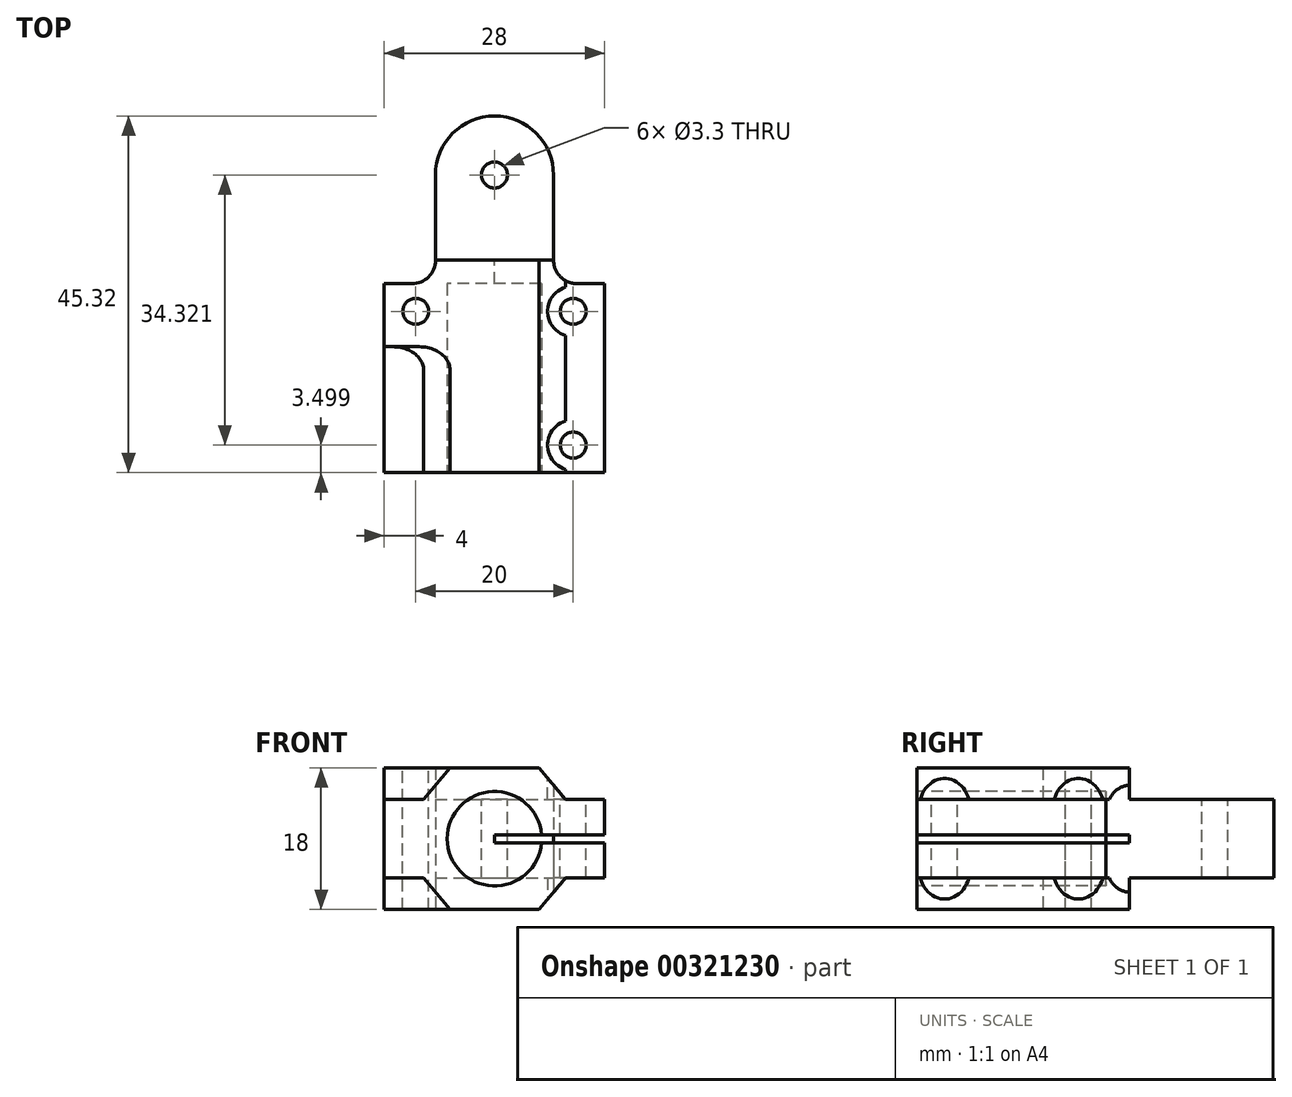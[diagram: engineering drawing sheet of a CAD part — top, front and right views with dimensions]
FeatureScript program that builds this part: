
annotation { "Feature Type Name" : "Feature", "Feature Type Description" : "" }
export const myFeature = defineFeature(function(context is Context, id is Id, definition is map)
    precondition{}
    {
        {
            var Q0;
            Q0=qCreatedBy(makeId("Top.planeOp"),FACE);
            var sketch = newSketch(context, id + "F0", { "sketchPlane" : qUnion([Q0])});
            skCircle(sketch, "E0", {"center": v(0, 0) * mm, "radius": 20 * mm, "construction": true});
            skSolve(sketch);
        }
        {
            var Q0;
            Q0=qCreatedBy(makeId("Top.planeOp"),FACE);
            var sketch = newSketch(context, id + "F1", { "sketchPlane" : qUnion([Q0])});
            skCircle(sketch, "E1", {"center": v(0, 0) * mm, "radius": 7.5 * mm});
            skLineSegment(sketch, "E2", {"start": v(-14, -13.82) * mm, "end": v(-14, -37.82) * mm});
            skLineSegment(sketch, "E3", {"start": v(-14, -37.82) * mm, "end": v(14, -37.82) * mm});
            skLineSegment(sketch, "E4", {"start": v(14, -37.82) * mm, "end": v(14, -13.82) * mm});
            skLineSegment(sketch, "E5", {"start": v(0, 0) * mm, "end": v(0, -37.82) * mm, "construction": true});
            skLineSegment(sketch, "E6", {"start": v(-6, -37.82) * mm, "end": v(-6, -10.4) * mm, "construction": true});
            skCircle(sketch, "E7.0", {"center": v(0, 0) * mm, "radius": 20 * mm, "construction": true});
            skPoint(sketch, "E8", {"position": v(-10, -17.32) * mm});
            skPoint(sketch, "E9.MirrorP", {"position": v(10, -17.32) * mm});
            skPoint(sketch, "E10", {"position": v(-10, -34.32) * mm});
            skPoint(sketch, "E11.MirrorP", {"position": v(10, -34.32) * mm});
            skLineSegment(sketch, "E12", {"start": v(-7.5, 0) * mm, "end": v(-7.5, -13.82) * mm});
            skLineSegment(sketch, "E13", {"start": v(-7.5, -13.82) * mm, "end": v(-14, -13.82) * mm});
            skLineSegment(sketch, "E14", {"start": v(7.5, 0) * mm, "end": v(7.5, -13.82) * mm});
            skLineSegment(sketch, "E15", {"start": v(7.5, -13.82) * mm, "end": v(14, -13.82) * mm});
            skLineSegment(sketch, "E16", {"start": v(-10, -17.32) * mm, "end": v(0, 0) * mm, "construction": true});
            skPoint(sketch, "E17", {"position": v(0, -34.32) * mm});
            skLineSegment(sketch, "E18", {"start": v(0, 0) * mm, "end": v(20, 0) * mm});
            skSolve(sketch);
        }
        {
            var Q0;
            Q0 = qSketchRegion(id + "F1", true);
            extrude(context, id + "F2", {"entities" : qUnion([Q0]), "endBound" : BoundingType.SYMMETRIC, "depth" : 18 * mm});
        }
        {
            var Q0;
            Q0=makeQuery(id+"F2.opExtrude","SWEPT_FACE",FACE,{"disambiguationData":[OSD([sQuery(id+"F1.wireOp",EDGE,"E3")])]});
            var sketch = newSketch(context, id + "F3", { "sketchPlane" : qUnion([Q0])});
            skCircle(sketch, "E19", {"center": v(0, 0) * mm, "radius": 6 * mm});
            skSolve(sketch);
        }
        {
            var Q0;
            Q0=makeQuery(id+"F3.imprint","IMPRINT",FACE,{"disambiguationData":[TD([[makeQuery(id+"F3.imprint","IMPRINT",EDGE,{"derivedFrom":sQuery(id+"F3.wireOp",EDGE,"E19")}),1.0]])]});
            var Q1;
            Q1=sQuery(id+"F3.wireOp",EDGE,"E19");
            extrude(context, id + "F4", {"entities" : qUnion([Q0]), "operationType" : NewBodyOperationType.REMOVE, "surfaceEntities" : qUnion([Q1]), "oppositeDirection" : true, "depth" : 24 * mm});
        }
        {
            var Q0;
            Q0=makeQuery(id+"F2.opExtrude","SWEPT_FACE",FACE,{"disambiguationData":[OSD([sQuery(id+"F1.wireOp",EDGE,"E3")])]});
            var sketch = newSketch(context, id + "F5", { "sketchPlane" : qUnion([Q0])});
            skLineSegment(sketch, "E20", {"start": v(0, 0) * mm, "end": v(0, 22.33) * mm, "construction": true});
            skLineSegment(sketch, "E21", {"start": v(0, 0) * mm, "end": v(-30.07, 0) * mm, "construction": true});
            skPoint(sketch, "E21.endSnap0", {"position": v(-14, 0) * mm});
            skLineSegment(sketch, "E22", {"start": v(5.64, 9) * mm, "end": v(9, 5) * mm});
            skLineSegment(sketch, "E23", {"start": v(9, 5) * mm, "end": v(14, 5) * mm});
            skLineSegment(sketch, "E24", {"start": v(5.64, 9) * mm, "end": v(14, 9) * mm});
            skLineSegment(sketch, "E25", {"start": v(14, 9) * mm, "end": v(14, 5) * mm});
            skLineSegment(sketch, "E26.MirrorCS", {"start": v(-5.64, 9) * mm, "end": v(-9, 5) * mm});
            skLineSegment(sketch, "E27.MirrorCS", {"start": v(-9, 5) * mm, "end": v(-14, 5) * mm});
            skLineSegment(sketch, "E28.MirrorCS", {"start": v(-14, 9) * mm, "end": v(-14, 5) * mm});
            skLineSegment(sketch, "E29.MirrorCS", {"start": v(-5.64, 9) * mm, "end": v(-14, 9) * mm});
            skLineSegment(sketch, "E30.MirrorCS", {"start": v(-5.64, -9) * mm, "end": v(-9, -5) * mm});
            skLineSegment(sketch, "E31.MirrorCS", {"start": v(-5.64, -9) * mm, "end": v(-14, -9) * mm});
            skLineSegment(sketch, "E32.MirrorCS", {"start": v(-14, -9) * mm, "end": v(-14, -5) * mm});
            skLineSegment(sketch, "E33.MirrorCS", {"start": v(-9, -5) * mm, "end": v(-14, -5) * mm});
            skLineSegment(sketch, "E34.MirrorCS", {"start": v(9, -5) * mm, "end": v(14, -5) * mm});
            skLineSegment(sketch, "E35.MirrorCS", {"start": v(5.64, -9) * mm, "end": v(9, -5) * mm});
            skLineSegment(sketch, "E36.MirrorCS", {"start": v(5.64, -9) * mm, "end": v(14, -9) * mm});
            skLineSegment(sketch, "E37.MirrorCS", {"start": v(14, -9) * mm, "end": v(14, -5) * mm});
            skSolve(sketch);
        }
        {
            var Q0;
            Q0=makeQuery(id+"F5.imprint","IMPRINT",FACE,{"disambiguationData":[TD([[makeQuery(id+"F5.imprint","IMPRINT",EDGE,{"derivedFrom":sQuery(id+"F5.wireOp",EDGE,"E22")}),1.0]])]});
            var Q1;
            Q1=makeQuery(id+"F5.imprint","IMPRINT",FACE,{"disambiguationData":[TD([[makeQuery(id+"F5.imprint","IMPRINT",EDGE,{"derivedFrom":sQuery(id+"F5.wireOp",EDGE,"E35.MirrorCS")}),-1.0]])]});
            extrude(context, id + "F6", {"entities" : qUnion([Q0, Q1]), "operationType" : NewBodyOperationType.REMOVE, "endBound" : BoundingType.THROUGH_ALL, "oppositeDirection" : true, "depth" : 30 * mm});
        }
        {
            var Q0;
            Q0=makeQuery(id+"F5.imprint","IMPRINT",FACE,{"disambiguationData":[TD([[makeQuery(id+"F5.imprint","IMPRINT",EDGE,{"derivedFrom":sQuery(id+"F5.wireOp",EDGE,"E26.MirrorCS")}),-1.0]])]});
            var Q1;
            Q1=makeQuery(id+"F5.imprint","IMPRINT",FACE,{"disambiguationData":[TD([[makeQuery(id+"F5.imprint","IMPRINT",EDGE,{"derivedFrom":sQuery(id+"F5.wireOp",EDGE,"E30.MirrorCS")}),1.0]])]});
            extrude(context, id + "F7", {"entities" : qUnion([Q0, Q1]), "operationType" : NewBodyOperationType.REMOVE, "oppositeDirection" : true, "depth" : 16 * mm});
        }
        {
            var Q0;
            Q0=makeQuery(id+"F2.opExtrude","SWEPT_EDGE",EDGE,{"disambiguationData":[OSD([sQuery(id+"F1.wireOp",EDGE,"E14"),sQuery(id+"F1.wireOp",EDGE,"E15")])]});
            var Q1;
            Q1=makeQuery(id+"F2.opExtrude","SWEPT_EDGE",EDGE,{"disambiguationData":[OSD([sQuery(id+"F1.wireOp",EDGE,"E12"),sQuery(id+"F1.wireOp",EDGE,"E13")])]});
            var Q2;
            Q2=makeQuery(id+"F7.boolean.opBoolean","COPY",EDGE,{"derivedFrom":makeQuery(id+"F7.opExtrude","CAP_EDGE",EDGE,{"disambiguationData":[OSD([sQuery(id+"F5.wireOp",EDGE,"E26.MirrorCS")])],"isStart":false})});
            var Q3;
            Q3=makeQuery(id+"F7.boolean.opBoolean","COPY",EDGE,{"derivedFrom":makeQuery(id+"F7.opExtrude","CAP_EDGE",EDGE,{"disambiguationData":[OSD([sQuery(id+"F5.wireOp",EDGE,"E30.MirrorCS")])],"isStart":false})});
            fillet(context, id + "F8", {"entities" : qUnion([Q0, Q1, Q2, Q3]), "radius" : 3 * mm, "tangentPropagation" : true, "allowEdgeOverflow" : false});
        }
        {
            var Q0;
            Q0=makeQuery(id+"F2.opExtrude","SWEPT_FACE",FACE,{"disambiguationData":[OSD([sQuery(id+"F1.wireOp",EDGE,"E14")])]});
            var sketch = newSketch(context, id + "F9", { "sketchPlane" : qUnion([Q0])});
            skLineSegment(sketch, "E38", {"start": v(0, 0) * mm, "end": v(12.2, 0) * mm, "construction": true});
            skLineSegment(sketch, "E39.0", {"start": v(4.94, 9) * mm, "end": v(-37.82, 9) * mm});
            skLineSegment(sketch, "E40.0", {"start": v(-10.82, 6.79) * mm, "end": v(-10.82, -6.79) * mm});
            skLineSegment(sketch, "E41.bottom", {"start": v(-10.82, 5) * mm, "end": v(9.93, 5) * mm});
            skLineSegment(sketch, "E41.top", {"start": v(-10.82, 9) * mm, "end": v(9.93, 9) * mm});
            skLineSegment(sketch, "E41.left", {"start": v(-10.82, 5) * mm, "end": v(-10.82, 9) * mm});
            skLineSegment(sketch, "E41.right", {"start": v(9.93, 5) * mm, "end": v(9.93, 9) * mm});
            skLineSegment(sketch, "E42.MirrorCS", {"start": v(-10.82, -5) * mm, "end": v(9.93, -5) * mm});
            skLineSegment(sketch, "E43.MirrorCS", {"start": v(9.93, -5) * mm, "end": v(9.93, -9) * mm});
            skLineSegment(sketch, "E44.MirrorCS", {"start": v(-10.82, -9) * mm, "end": v(9.93, -9) * mm});
            skLineSegment(sketch, "E45.MirrorCS", {"start": v(-10.82, -5) * mm, "end": v(-10.82, -9) * mm});
            skSolve(sketch);
        }
        {
            var Q0;
            Q0 = qSketchRegion(id + "F9", true);
            extrude(context, id + "F10", {"entities" : qUnion([Q0]), "operationType" : NewBodyOperationType.REMOVE, "endBound" : BoundingType.THROUGH_ALL, "oppositeDirection" : true, "depth" : 25 * mm});
        }
        {
            var Q0;
            Q0=makeQuery(id+"F2.opExtrude","CAP_FACE",FACE,{"disambiguationData":[OSD([sQuery(id+"F1.wireOp",EDGE,"E1"),sQuery(id+"F1.wireOp",EDGE,"FBtvDSVI-ImC7-X96t-MR7d-RFuTRP7ZC0sh"),sQuery(id+"F1.wireOp",EDGE,"E2"),sQuery(id+"F1.wireOp",EDGE,"E3"),sQuery(id+"F1.wireOp",EDGE,"E4"),sQuery(id+"F1.wireOp",EDGE,"JECMxVH1-krey-lWLA-VkQH-IbSMAUhGZjWj")])],"isStart":false});
            var sketch = newSketch(context, id + "F11", { "sketchPlane" : qUnion([Q0])});
            skPoint(sketch, "E46.0", {"position": v(-10, -17.32) * mm});
            skPoint(sketch, "E46.1", {"position": v(-10, -34.32) * mm});
            skPoint(sketch, "E46.2", {"position": v(10, -34.32) * mm});
            skPoint(sketch, "E46.3", {"position": v(10, -17.32) * mm});
            skPoint(sketch, "E47.0", {"position": v(0, 0) * mm});
            skSolve(sketch);
        }
        {
            var Q0;
            Q0=sQuery(id+"F11.wireOp",VERTEX,"E46.2");
            var Q1;
            Q1=sQuery(id+"F11.wireOp",VERTEX,"E46.3");
            var Q2;
            Q2=sQuery(id+"F11.wireOp",VERTEX,"E47.0");
            var Q3;
            Q3=sQuery(id+"F11.wireOp",VERTEX,"E46.0");
            var Q4;
            Q4=makeQuery(id+"F2.opExtrude","SWEPT_BODY",BODY,{"disambiguationData":[OSD([sQuery(id+"F1.wireOp",EDGE,"E1"),sQuery(id+"F1.wireOp",EDGE,"FBtvDSVI-ImC7-X96t-MR7d-RFuTRP7ZC0sh"),sQuery(id+"F1.wireOp",EDGE,"E2"),sQuery(id+"F1.wireOp",EDGE,"E3"),sQuery(id+"F1.wireOp",EDGE,"E4"),sQuery(id+"F1.wireOp",EDGE,"JECMxVH1-krey-lWLA-VkQH-IbSMAUhGZjWj")])]});
            hole(context, id + "F12", {"style" : HoleStyle.C_BORE, "endStyle" : HoleEndStyle.THROUGH, "holeDiameter" : 3.3 * mm, "cBoreDiameter" : 6.5 * mm, "cBoreDepth" : 0 * mm, "tappedDepth" : 1.2 * mm, "tapClearance" : 3, "locations" : qUnion([Q0, Q1, Q2, Q3]), "scope" : qUnion([Q4])});
        }
        {
            var Q0;
            Q0=makeQuery(id+"F2.opExtrude","CAP_FACE",FACE,{"disambiguationData":[OSD([sQuery(id+"F1.wireOp",EDGE,"E1"),sQuery(id+"F1.wireOp",EDGE,"E2"),sQuery(id+"F1.wireOp",EDGE,"E3"),sQuery(id+"F1.wireOp",EDGE,"E4"),sQuery(id+"F1.wireOp",EDGE,"E12"),sQuery(id+"F1.wireOp",EDGE,"E13"),sQuery(id+"F1.wireOp",EDGE,"E14"),sQuery(id+"F1.wireOp",EDGE,"E15")])],"isStart":true});
            var sketch = newSketch(context, id + "F13", { "sketchPlane" : qUnion([Q0])});
            skPoint(sketch, "E48.0", {"position": v(-10, 34.32) * mm});
            skPoint(sketch, "E48.1", {"position": v(-10, 17.32) * mm});
            skPoint(sketch, "E48.2", {"position": v(10, 17.32) * mm});
            skPoint(sketch, "E48.3", {"position": v(10, 34.32) * mm});
            skSolve(sketch);
        }
        {
            var Q0;
            Q0=sQuery(id+"F13.wireOp",VERTEX,"E48.3");
            var Q1;
            Q1=sQuery(id+"F13.wireOp",VERTEX,"E48.2");
            var Q2;
            Q2=makeQuery(id+"F2.opExtrude","SWEPT_BODY",BODY,{"disambiguationData":[OSD([sQuery(id+"F1.wireOp",EDGE,"E1"),sQuery(id+"F1.wireOp",EDGE,"E2"),sQuery(id+"F1.wireOp",EDGE,"E3"),sQuery(id+"F1.wireOp",EDGE,"E4"),sQuery(id+"F1.wireOp",EDGE,"E12"),sQuery(id+"F1.wireOp",EDGE,"E13"),sQuery(id+"F1.wireOp",EDGE,"E14"),sQuery(id+"F1.wireOp",EDGE,"E15")])]});
            hole(context, id + "F14", {"style" : HoleStyle.C_BORE, "endStyle" : HoleEndStyle.THROUGH, "holeDiameter" : 3.3 * mm, "cBoreDiameter" : 6.5 * mm, "cBoreDepth" : 0 * mm, "tappedDepth" : 1.2 * mm, "tapClearance" : 3, "locations" : qUnion([Q0, Q1]), "scope" : qUnion([Q2])});
        }
        {
            var Q0;
            Q0=qCreatedBy(makeId("Right.planeOp"),FACE);
            var sketch = newSketch(context, id + "F15", { "sketchPlane" : qUnion([Q0])});
            skLineSegment(sketch, "E49", {"start": v(-37.82, 0.5) * mm, "end": v(-10.82, 0.5) * mm});
            skLineSegment(sketch, "E50", {"start": v(-10.82, -0.5) * mm, "end": v(-37.82, -0.5) * mm});
            skLineSegment(sketch, "E51", {"start": v(-37.82, -0.5) * mm, "end": v(-37.82, 0.5) * mm});
            skLineSegment(sketch, "E52", {"start": v(0, 0) * mm, "end": v(-48.15, 0) * mm, "construction": true});
            skLineSegment(sketch, "E53", {"start": v(-10.82, 0.5) * mm, "end": v(-10.82, -0.5) * mm});
            skLineSegment(sketch, "E54.0", {"start": v(-10.82, 5) * mm, "end": v(-10.82, -5) * mm});
            skSolve(sketch);
        }
        {
            var Q0;
            Q0 = qSketchRegion(id + "F15", true);
            var Q1;
            Q1=makeQuery(id+"F2.opExtrude","SWEPT_BODY",BODY,{"disambiguationData":[OSD([sQuery(id+"F1.wireOp",EDGE,"E1"),sQuery(id+"F1.wireOp",EDGE,"E2"),sQuery(id+"F1.wireOp",EDGE,"E3"),sQuery(id+"F1.wireOp",EDGE,"E4"),sQuery(id+"F1.wireOp",EDGE,"E12"),sQuery(id+"F1.wireOp",EDGE,"E13"),sQuery(id+"F1.wireOp",EDGE,"E14"),sQuery(id+"F1.wireOp",EDGE,"E15")])]});
            extrude(context, id + "F16", {"entities" : qUnion([Q0]), "operationType" : NewBodyOperationType.REMOVE, "endBoundEntityBody" : qUnion([Q1]), "depth" : 30 * mm});
        }
    });
